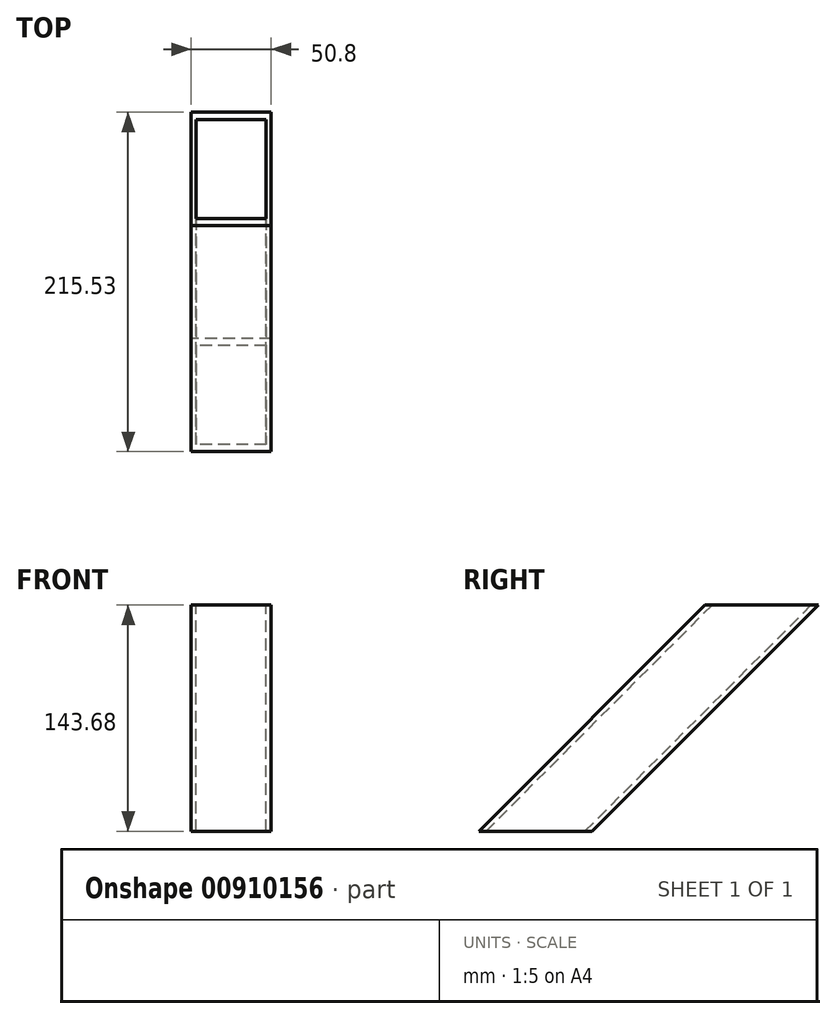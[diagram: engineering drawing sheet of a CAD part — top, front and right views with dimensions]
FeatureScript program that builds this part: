
annotation { "Feature Type Name" : "Feature", "Feature Type Description" : "" }
export const myFeature = defineFeature(function(context is Context, id is Id, definition is map)
    precondition{}
    {
        {
            var Q0;
            Q0=qCreatedBy(makeId("Right.planeOp"),FACE);
            var sketch = newSketch(context, id + "F0", { "sketchPlane" : qUnion([Q0])});
            skLineSegment(sketch, "E0", {"start": v(8.38, 45.63) * mm, "end": v(80.23, 45.63) * mm});
            skLineSegment(sketch, "E1", {"start": v(80.23, 45.63) * mm, "end": v(-63.46, -98.05) * mm});
            skLineSegment(sketch, "E2", {"start": v(-63.46, -98.05) * mm, "end": v(-135.3, -98.05) * mm});
            skLineSegment(sketch, "E3", {"start": v(-135.3, -98.05) * mm, "end": v(8.38, 45.63) * mm});
            skSolve(sketch);
        }
        {
            var Q0;
            Q0=makeQuery(id+"F0.imprint","IMPRINT",FACE,{"disambiguationData":[TD([[makeQuery(id+"F0.imprint","IMPRINT",EDGE,{"derivedFrom":sQuery(id+"F0.wireOp",EDGE,"E0")}),-1.0]])]});
            extrude(context, id + "F1", {"entities" : qUnion([Q0]), "depth" : 50.8 * mm, "offsetDistance" : 25.4 * mm});
        }
        {
            var Q0;
            Q0=makeQuery(id+"F1.opExtrude","SWEPT_FACE",FACE,{"disambiguationData":[OSD([sQuery(id+"F0.wireOp",EDGE,"E0")])]});
            var Q1;
            Q1=makeQuery(id+"F1.opExtrude","SWEPT_FACE",FACE,{"disambiguationData":[OSD([sQuery(id+"F0.wireOp",EDGE,"E2")])]});
            shell(context, id + "F2", {"entities" : qUnion([Q0, Q1]), "thickness" : 3.17 * mm});
        }
    });
